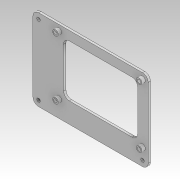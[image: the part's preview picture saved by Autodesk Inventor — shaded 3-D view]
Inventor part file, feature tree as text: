
AUTODESK INVENTOR PART (.ipt)
format: ipt  version: 2020 (Build 240168000, 168)  size: 146,944 bytes
history: native  units: mm
features: extrude x2, sketch x2
ambient origin geometry x8: Origin, YZ Plane, XZ Plane, XY Plane, X Axis, Y Axis, Z Axis, Center Point
bodies: Solid1 (feature_tree)
feature tree (4):
  extrude  "Extrusion1"  Depth=3.0mm
  extrude  "Extrusion2"  Depth=5.0mm
  sketch  "Sketch1"  dims[d0=74.1mm d1=52.0mm d2=3.0mm d3=45.0mm d4=6.0mm d5=0.0mm d8=62.0mm]
  sketch  "Sketch2"  dims[d9=92.0mm d10=5.0mm d11=5.0mm d12=5.0mm d13=5.0mm d14=5.0mm d15=5.0mm d16=3.0mm d17=2.0mm d18=0.0mm d19=5.0mm d20=3.0mm d21=0.0mm]
